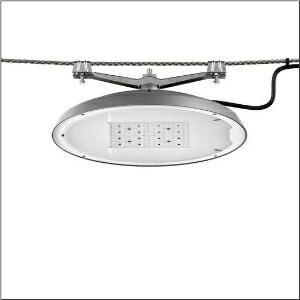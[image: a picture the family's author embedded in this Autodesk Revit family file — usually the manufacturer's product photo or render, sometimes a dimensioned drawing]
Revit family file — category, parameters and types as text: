
# Revit family: dl_r__50_iq_mini___st0_8s_5xa248v41f08le_55a3
name_source: partatom
category: Lighting Fixtures
units: mm (PartAtom-declared; Revit-internal decimal feet)

## family parameters
Cut with Voids When Loaded = No
Host = Face
Light Source = No
Part Type = Normal
Room Calculation Point = No
Round Connector Dimension = Use Diameter
Shared = No

## types (1)
- --- (1 x LED, 10390 lm, 64.1 W, 4000K)
    Apparent Load = 64 VA
    CIE Flux Codes = 38 75 97 100 100
    Color Rendering = 70
    Color Temperature = 4000K
    Default Elevation = 1800 mm
    Description = DL® 50 iQ mini, catenary luminaire, primary light control with lens, of PMMA, primary optical cover: cover, of toughened safety glass, transparent, light distribution: ST0.8s, light emission: direct distribution, primary light characteristic: symmetric, installation type: suspended mounting, LED, High Power LED, rated luminous flux: 10.390lm, luminous efficacy: 162lm/W, light colour: 740, colour temperature: 4000K, control gear: iQ Street-Remote, control: optimised constant luminous flux control (CLO 2.0), Desk-Remote (wireless, voltage-free reading and setting of iQ features in the workshop via application-optimized NFC function/RFID function), Light-Fading, Smart-Wire, Night-Set, Lumen-Switch, Temp-Guard, Auto-Match, Street-Remote, mains connection: 230..240V, AC, 50/60Hz, start of lifetime: 64W, end of service life: 67W, reduction: 30W, luminaire housing, of diecast aluminium, powder-coated, Siteco® metallic grey (DB 702S), diameter: 500mm, height: 115mm, mounting height: 4..12m, protection rating (complete): IP66, insulation class (complete): insulation class II (safety insulation), certification: CE, ENEC, ENEC+, VDE, impact resistance: IK08, permissible operating ambient temperature for outdoor applications: -25..+40°C, standard-compliant lighting for roads and squares, packaging unit: 1 piece

Light Distribution: ST0.8s
    Height = 124 mm  [stored 0.406824 ft]
    Lamp = 1 x LED
    Lamp Light Flux = 10390 lm
    Lamp Power = 64.1 W
    Lamp count = 1
    Length = 500 mm
    Luminous efficacy = 162 lm/W
    Manufacturer = Siteco
    ModVariant = No
    Model = 5XA248V41F08LE
    Number of Poles = 1
    OnlyDefault = Yes
    Power Factor = 1
    Product Name = DL® 50 iQ mini | ST0.8s
    Product group = catenary luminaire
    ProductGroupID = 6300
    Protection Class = Protection class II
    Protection Degree = IP 66
    RLX_Detail_Level = 1
    RLX_Emergency_Light_Flux = 0 lm
    RLX_Emergency_Type = 0
    RLX_Emergency_Type_DB = No
    RlxData = <blob elided: 127797 chars, md5=0ad77a02>
    Socket = socket
    Standby Power = 0 W
    System Light Flux = 10390 lm
    System Power = 64 W
    Type Comments = factory setting: luminous flux: 100 % | dim-lin: 254 | 672 mA
    Type Image = l_1251783.jpg
    URL = http://relux.com
    VarID = @adj_141020
    Voltage = 0 V
    Weight = 0.00 kg
    Width = 0 mm  [stored 0 ft]

note: [stored X ft] marks values corroborated as IEEE doubles in the binary element streams (Revit-internal decimal feet)

## geometry (parser evidence)
native form markers: Blend x4, Sweep x15
no freeform markers — native parametric forms only
